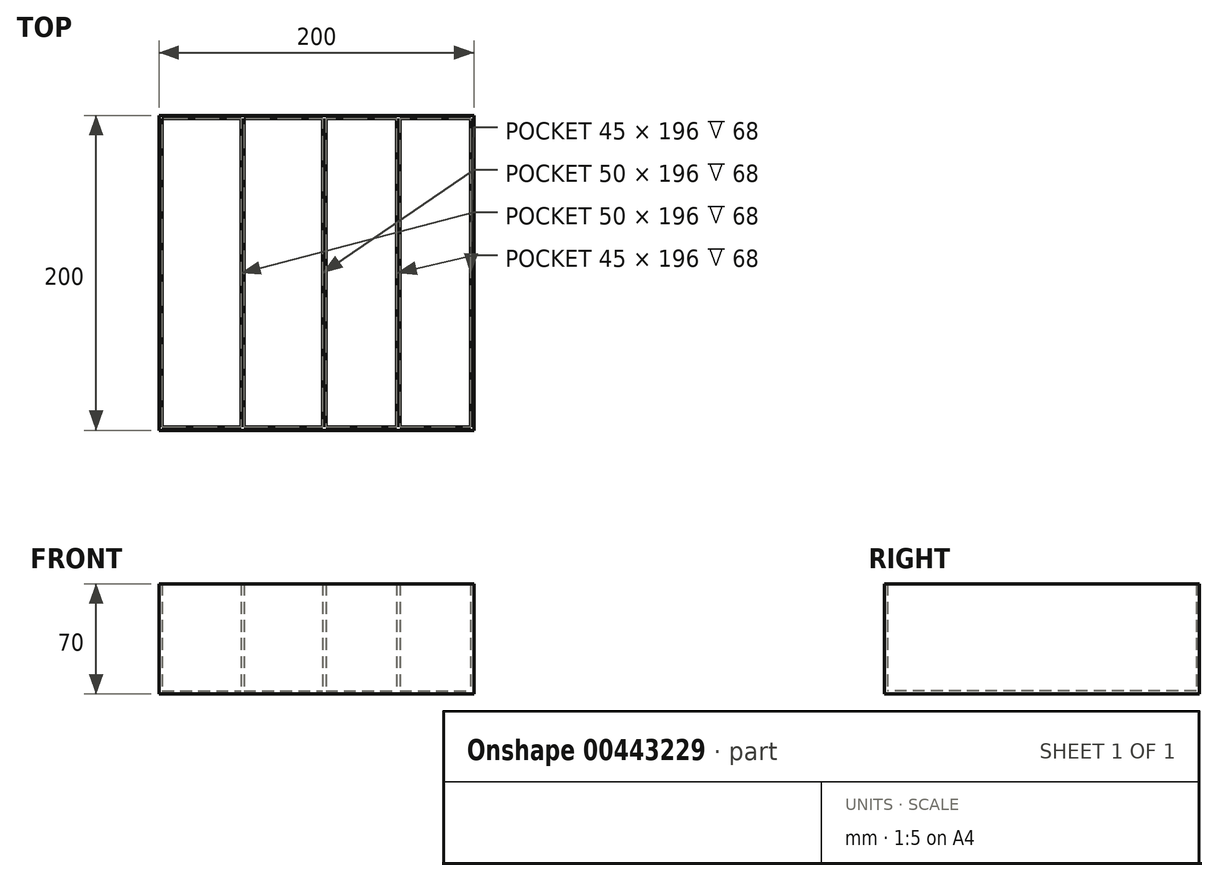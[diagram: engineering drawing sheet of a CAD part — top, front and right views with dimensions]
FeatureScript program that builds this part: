
annotation { "Feature Type Name" : "Feature", "Feature Type Description" : "" }
export const myFeature = defineFeature(function(context is Context, id is Id, definition is map)
    precondition{}
    {
        {
            var Q0;
            Q0=qCreatedBy(makeId("Top.planeOp"),FACE);
            var sketch = newSketch(context, id + "F0", { "sketchPlane" : qUnion([Q0])});
            skLineSegment(sketch, "E0.bottom", {"start": v(-108, 66.12) * mm, "end": v(92, 66.12) * mm});
            skLineSegment(sketch, "E0.top", {"start": v(-108, -133.88) * mm, "end": v(92, -133.88) * mm});
            skLineSegment(sketch, "E0.left", {"start": v(-108, 66.12) * mm, "end": v(-108, -133.88) * mm});
            skLineSegment(sketch, "E0.right", {"start": v(92, 66.12) * mm, "end": v(92, -133.88) * mm});
            skSolve(sketch);
        }
        {
            var Q0;
            Q0=makeQuery(id+"F0.imprint","IMPRINT",FACE,{"disambiguationData":[TD([[makeQuery(id+"F0.imprint","IMPRINT",EDGE,{"derivedFrom":sQuery(id+"F0.wireOp",EDGE,"E0.bottom")}),-1.0]])]});
            extrude(context, id + "F1", {"entities" : qUnion([Q0]), "depth" : 70 * mm, "offsetDistance" : 25 * mm});
        }
        {
            var Q0;
            Q0=makeQuery(id+"F1.opExtrude","CAP_FACE",FACE,{"disambiguationData":[OSD([sQuery(id+"F0.wireOp",EDGE,"E0.bottom"),sQuery(id+"F0.wireOp",EDGE,"E0.top"),sQuery(id+"F0.wireOp",EDGE,"E0.left"),sQuery(id+"F0.wireOp",EDGE,"E0.right")])],"isStart":false});
            shell(context, id + "F2", {"entities" : qUnion([Q0]), "thickness" : 2 * mm});
        }
        {
            var Q0;
            Q0=makeQuery(id+"F2.opShell","OFFSET_FACE",FACE,{"disambiguationData":[OSD([sQuery(id+"F0.wireOp",EDGE,"E0.bottom"),sQuery(id+"F0.wireOp",EDGE,"E0.top"),sQuery(id+"F0.wireOp",EDGE,"E0.left"),sQuery(id+"F0.wireOp",EDGE,"E0.right")])]});
            var sketch = newSketch(context, id + "F3", { "sketchPlane" : qUnion([Q0])});
            skLineSegment(sketch, "E1", {"start": v(-56, -131.88) * mm, "end": v(-56, 64.12) * mm});
            skLineSegment(sketch, "E2", {"start": v(-2, -131.88) * mm, "end": v(-2, 64.12) * mm});
            skLineSegment(sketch, "E3", {"start": v(43, 64.12) * mm, "end": v(43, -131.88) * mm});
            skLineSegment(sketch, "E4", {"start": v(-54, 64.12) * mm, "end": v(-54, -131.88) * mm});
            skLineSegment(sketch, "E5", {"start": v(-4, 64.12) * mm, "end": v(-4, -131.88) * mm});
            skLineSegment(sketch, "E6", {"start": v(45, 64.12) * mm, "end": v(45, -131.88) * mm});
            skSolve(sketch);
        }
        {
            var Q0;
            {var subQ0=sQuery(id+"F3.wireOp",EDGE,"E1");Q0=makeQuery(id+"F3.imprint","IMPRINT",FACE,{"disambiguationData":[TD([[makeQuery(id+"F3.imprint","IMPRINT",EDGE,{"derivedFrom":subQ0}),-1.0]])]});}
            var Q1;
            {var subQ0=sQuery(id+"F3.wireOp",EDGE,"E2");Q1=makeQuery(id+"F3.imprint","IMPRINT",FACE,{"disambiguationData":[TD([[makeQuery(id+"F3.imprint","IMPRINT",EDGE,{"derivedFrom":subQ0}),1.0]])]});}
            var Q2;
            {var subQ0=sQuery(id+"F3.wireOp",EDGE,"E3");Q2=makeQuery(id+"F3.imprint","IMPRINT",FACE,{"disambiguationData":[TD([[makeQuery(id+"F3.imprint","IMPRINT",EDGE,{"derivedFrom":subQ0}),1.0]])]});}
            extrude(context, id + "F4", {"entities" : qUnion([Q0, Q1, Q2]), "operationType" : NewBodyOperationType.ADD, "depth" : 68 * mm, "offsetDistance" : 25 * mm});
        }
    });
